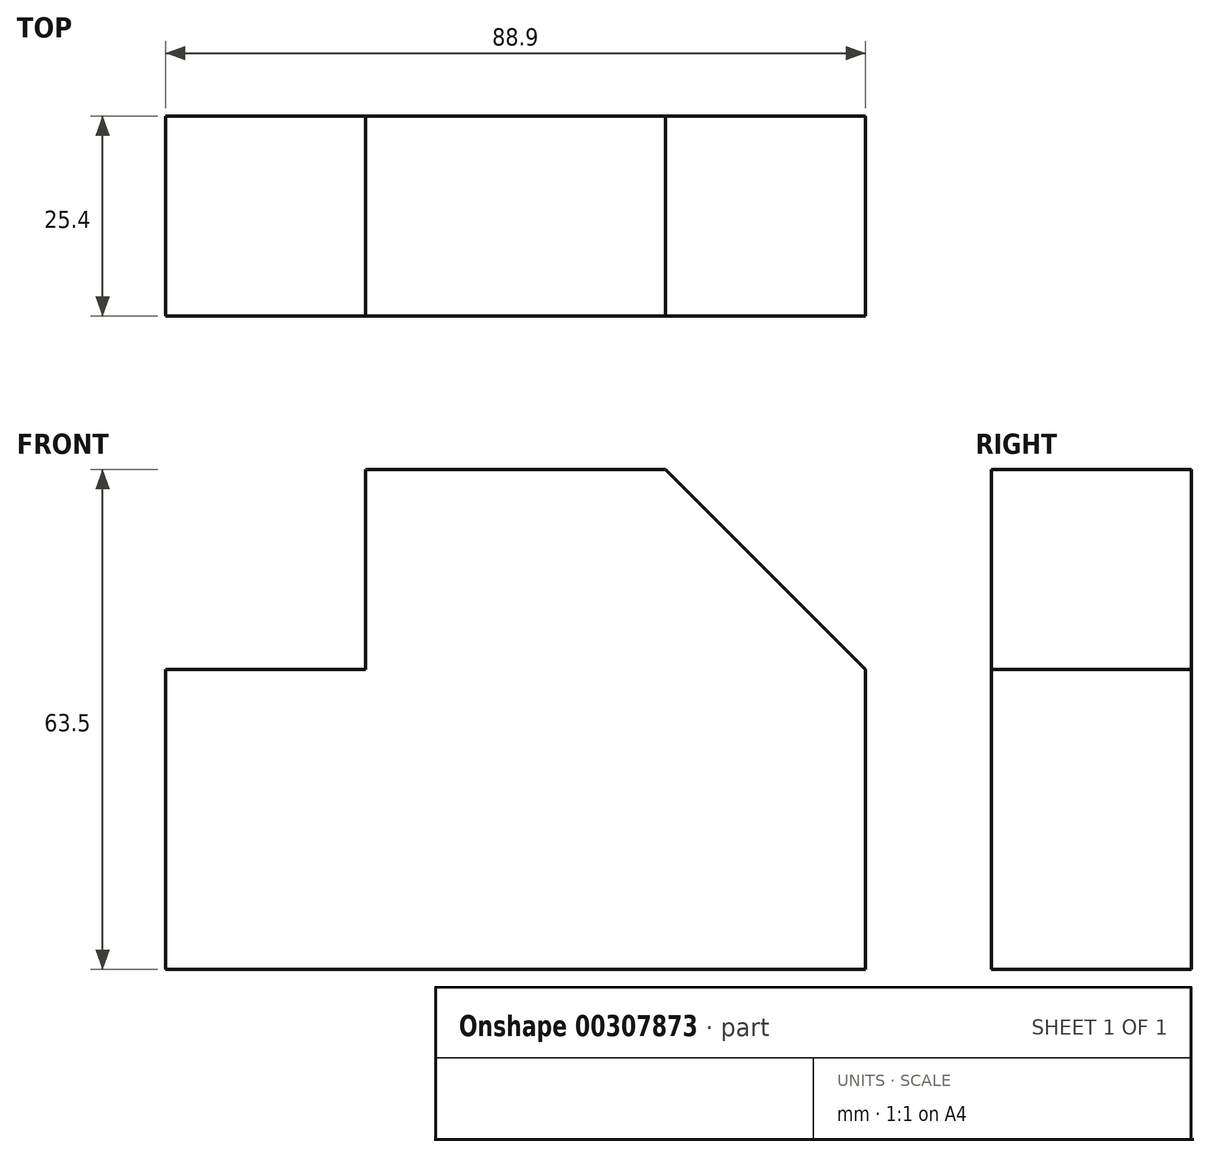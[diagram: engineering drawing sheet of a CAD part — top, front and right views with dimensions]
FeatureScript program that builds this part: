
annotation { "Feature Type Name" : "Feature", "Feature Type Description" : "" }
export const myFeature = defineFeature(function(context is Context, id is Id, definition is map)
    precondition{}
    {
        {
            var Q0;
            Q0=qCreatedBy(makeId("Front.planeOp"),FACE);
            var sketch = newSketch(context, id + "F0", { "sketchPlane" : qUnion([Q0])});
            skLineSegment(sketch, "E0", {"start": v(-55, 25.11) * mm, "end": v(-55, -12.99) * mm});
            skLineSegment(sketch, "E1", {"start": v(-55, -12.99) * mm, "end": v(33.9, -12.99) * mm});
            skLineSegment(sketch, "E2", {"start": v(-55, 25.11) * mm, "end": v(-29.6, 25.11) * mm});
            skLineSegment(sketch, "E3", {"start": v(-29.6, 25.11) * mm, "end": v(-29.6, 50.51) * mm});
            skLineSegment(sketch, "E4", {"start": v(-29.6, 50.51) * mm, "end": v(8.5, 50.51) * mm});
            skLineSegment(sketch, "E5", {"start": v(33.9, -12.99) * mm, "end": v(33.9, 25.11) * mm});
            skLineSegment(sketch, "E6", {"start": v(8.5, 50.51) * mm, "end": v(33.9, 25.11) * mm});
            skSolve(sketch);
        }
        {
            var Q0;
            Q0=makeQuery(id+"F0.imprint","IMPRINT",FACE,{"disambiguationData":[TD([[makeQuery(id+"F0.imprint","IMPRINT",EDGE,{"derivedFrom":sQuery(id+"F0.wireOp",EDGE,"E0")}),1.0]])]});
            extrude(context, id + "F1", {"entities" : qUnion([Q0]), "depth" : 25.4 * mm});
        }
    });
